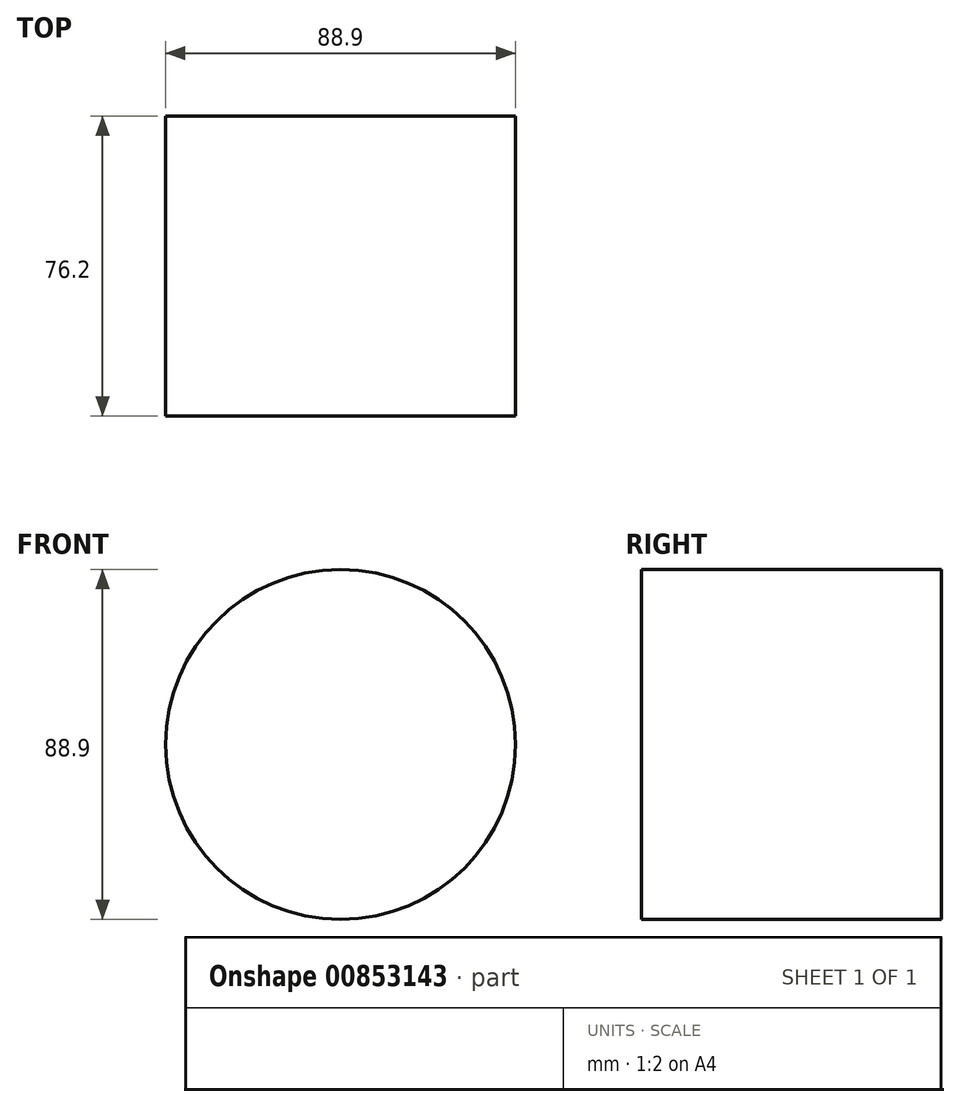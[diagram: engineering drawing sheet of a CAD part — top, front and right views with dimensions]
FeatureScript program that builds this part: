
annotation { "Feature Type Name" : "Feature", "Feature Type Description" : "" }
export const myFeature = defineFeature(function(context is Context, id is Id, definition is map)
    precondition{}
    {
        {
            var Q0;
            Q0=qCreatedBy(makeId("Front.planeOp"),FACE);
            var sketch = newSketch(context, id + "F0", { "sketchPlane" : qUnion([Q0])});
            skCircle(sketch, "E0", {"center": v(0, 0) * mm, "radius": 44.45 * mm});
            skSolve(sketch);
        }
        {
            var Q0;
            Q0=makeQuery(id+"F0.imprint","IMPRINT",FACE,{"disambiguationData":[TD([[makeQuery(id+"F0.imprint","IMPRINT",EDGE,{"derivedFrom":sQuery(id+"F0.wireOp",EDGE,"E0")}),1.0]])]});
            extrude(context, id + "F1", {"entities" : qUnion([Q0]), "oppositeDirection" : true, "depth" : 76.2 * mm, "offsetDistance" : 25.4 * mm});
        }
    });
